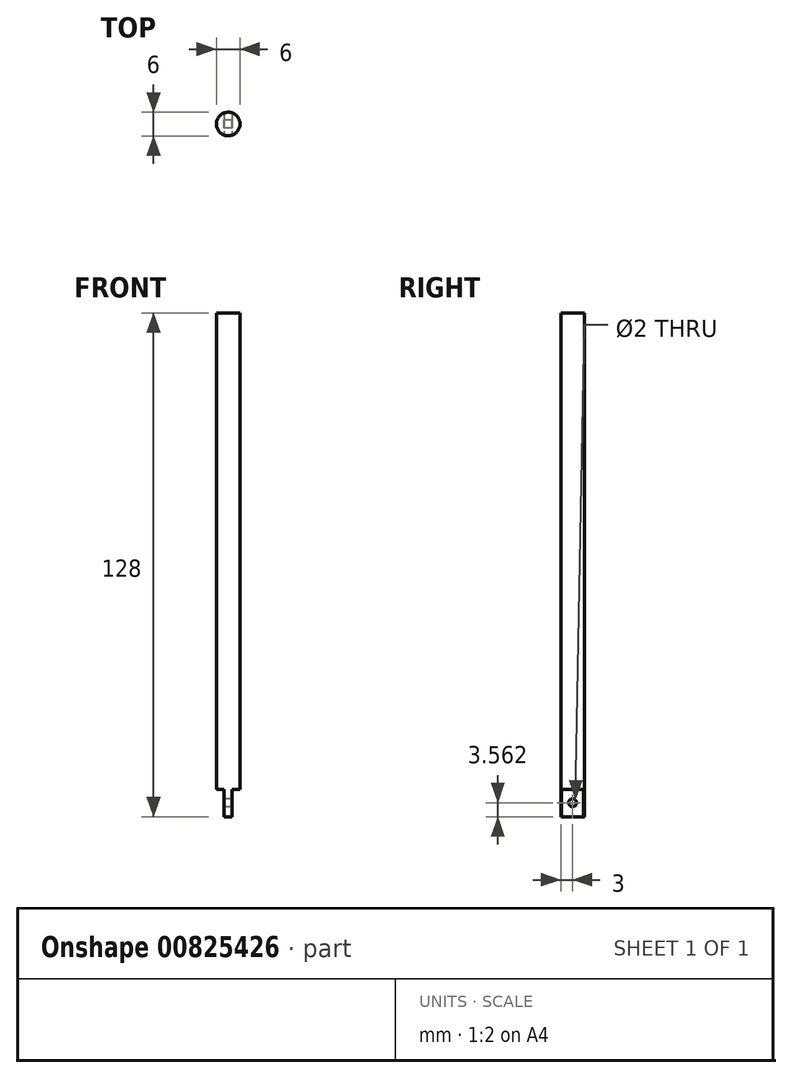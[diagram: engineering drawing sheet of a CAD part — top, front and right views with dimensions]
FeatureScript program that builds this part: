
annotation { "Feature Type Name" : "Feature", "Feature Type Description" : "" }
export const myFeature = defineFeature(function(context is Context, id is Id, definition is map)
    precondition{}
    {
        {
            var Q0;
            Q0=qCreatedBy(makeId("Top.planeOp"),FACE);
            var sketch = newSketch(context, id + "F0", { "sketchPlane" : qUnion([Q0])});
            skCircle(sketch, "E0", {"center": v(0, 0) * mm, "radius": 3 * mm});
            skSolve(sketch);
        }
        {
            var Q0;
            Q0=makeQuery(id+"F0.imprint","IMPRINT",FACE,{"disambiguationData":[TD([[makeQuery(id+"F0.imprint","IMPRINT",EDGE,{"derivedFrom":sQuery(id+"F0.wireOp",EDGE,"E0")}),1.0]])]});
            var Q1;
            Q1=sQuery(id+"F0.wireOp",EDGE,"E0");
            extrude(context, id + "F1", {"entities" : qUnion([Q0]), "surfaceEntities" : qUnion([Q1]), "depth" : 128 * mm, "offsetDistance" : 25 * mm});
        }
        {
            var Q0;
            Q0=qCreatedBy(makeId("Front.planeOp"),FACE);
            var sketch = newSketch(context, id + "F2", { "sketchPlane" : qUnion([Q0])});
            skLineSegment(sketch, "E1", {"start": v(0, 0) * mm, "end": v(0, 22.17) * mm, "construction": true});
            skLineSegment(sketch, "E2", {"start": v(1, 0) * mm, "end": v(7.55, 0) * mm, "construction": true});
            skLineSegment(sketch, "E3", {"start": v(-1, 0) * mm, "end": v(-8.68, 0) * mm, "construction": true});
            skLineSegment(sketch, "E4.bottom", {"start": v(0, 0) * mm, "end": v(-1, 0) * mm});
            skLineSegment(sketch, "E4.left", {"start": v(0, 0) * mm, "end": v(0, 7) * mm});
            skLineSegment(sketch, "E4.right", {"start": v(-1, 0) * mm, "end": v(-1, 7) * mm});
            skLineSegment(sketch, "E5.MirrorCS", {"start": v(1, 0) * mm, "end": v(1, 7) * mm});
            skLineSegment(sketch, "E6", {"start": v(-1, 7) * mm, "end": v(-3, 7) * mm});
            skLineSegment(sketch, "E7", {"start": v(-3, 7) * mm, "end": v(-3, 0) * mm});
            skLineSegment(sketch, "E8", {"start": v(-3, 0) * mm, "end": v(-1, 0) * mm});
            skLineSegment(sketch, "E9", {"start": v(1, 7) * mm, "end": v(3, 7) * mm});
            skLineSegment(sketch, "E10", {"start": v(3, 7) * mm, "end": v(3, 0) * mm});
            skLineSegment(sketch, "E11", {"start": v(3, 0) * mm, "end": v(1, 0) * mm});
            skPoint(sketch, "E12.MirrorCS.start.orphan", {"position": v(0, 7) * mm});
            skLineSegment(sketch, "E13", {"start": v(1, 0) * mm, "end": v(3, 0) * mm});
            skSolve(sketch);
        }
        {
            var Q0;
            Q0 = qSketchRegion(id + "F2", true);
            extrude(context, id + "F3", {"entities" : qUnion([Q0]), "operationType" : NewBodyOperationType.REMOVE, "endBound" : BoundingType.SYMMETRIC, "oppositeDirection" : true, "depth" : 25 * mm, "offsetDistance" : 25 * mm});
        }
        {
            var Q0;
            Q0=qCreatedBy(makeId("Right.planeOp"),FACE);
            var sketch = newSketch(context, id + "F4", { "sketchPlane" : qUnion([Q0])});
            skLineSegment(sketch, "E14", {"start": v(0, 0) * mm, "end": v(0, 7.12) * mm, "construction": true});
            skCircle(sketch, "E15", {"center": v(0, 3.56) * mm, "radius": 1 * mm});
            skSolve(sketch);
        }
        {
            var Q0;
            Q0=makeQuery(id+"F4.imprint","IMPRINT",FACE,{"disambiguationData":[TD([[makeQuery(id+"F4.imprint","IMPRINT",EDGE,{"derivedFrom":sQuery(id+"F4.wireOp",EDGE,"E15")}),1.0]])]});
            extrude(context, id + "F5", {"entities" : qUnion([Q0]), "operationType" : NewBodyOperationType.REMOVE, "endBound" : BoundingType.SYMMETRIC, "depth" : 100 * mm, "offsetDistance" : 25 * mm});
        }
    });
